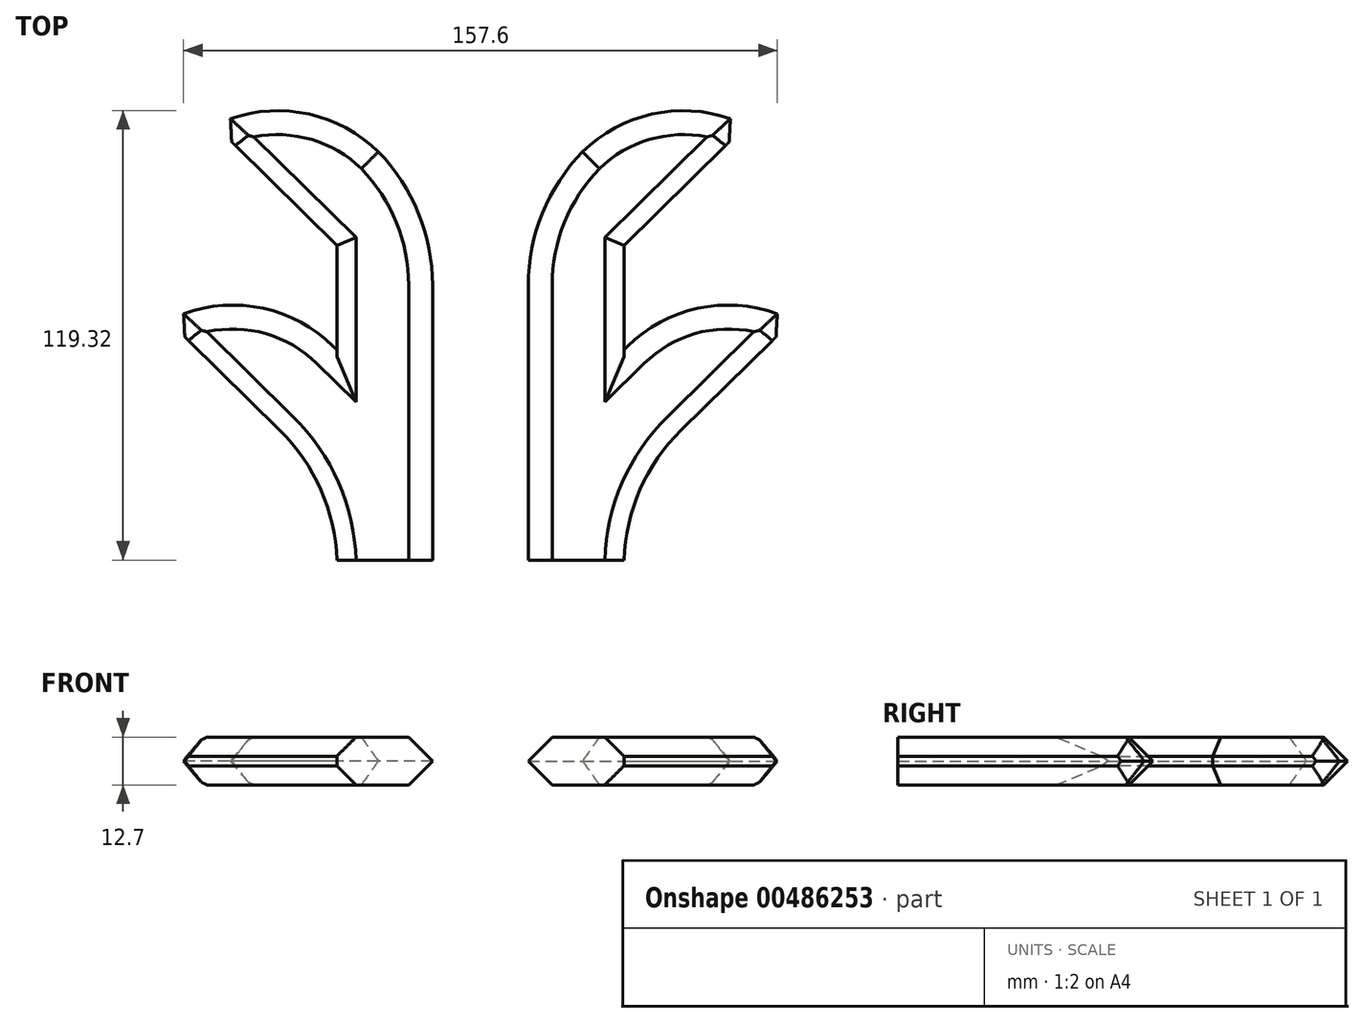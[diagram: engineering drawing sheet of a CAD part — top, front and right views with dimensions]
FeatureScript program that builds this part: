
annotation { "Feature Type Name" : "Feature", "Feature Type Description" : "" }
export const myFeature = defineFeature(function(context is Context, id is Id, definition is map)
    precondition{}
    {
        {
            var Q0;
            Q0=qCreatedBy(makeId("Top.planeOp"),FACE);
            var sketch = newSketch(context, id + "F0", { "sketchPlane" : qUnion([Q0])});
            skLineSegment(sketch, "E0.0", {"start": v(12.7, 94.22) * mm, "end": v(-27.32, 133.57) * mm});
            skLineSegment(sketch, "E1.0", {"start": v(-12.7, 83.58) * mm, "end": v(-45.13, 115.46) * mm});
            skLineSegment(sketch, "E2.0", {"start": v(12.7, 0) * mm, "end": v(12.7, 94.22) * mm});
            skLineSegment(sketch, "E3.0", {"start": v(-12.7, 0) * mm, "end": v(-12.7, 19.58) * mm});
            skLineSegment(sketch, "E4.0", {"start": v(-12.7, 55.85) * mm, "end": v(-39.37, 82.07) * mm});
            skLineSegment(sketch, "E5.0", {"start": v(-12.7, 19.58) * mm, "end": v(-57.5, 63.62) * mm});
            skLineSegment(sketch, "E6", {"start": v(-45.13, 115.46) * mm, "end": v(-27.32, 133.57) * mm});
            skLineSegment(sketch, "E7", {"start": v(-12.7, 0) * mm, "end": v(12.7, 0) * mm});
            skLineSegment(sketch, "E8.trimOffspring", {"start": v(-12.7, 55.85) * mm, "end": v(-12.7, 83.58) * mm});
            skLineSegment(sketch, "E9.0", {"start": v(-57.5, 63.62) * mm, "end": v(-39.37, 82.07) * mm});
            skSolve(sketch);
        }
        {
            var Q0;
            Q0=makeQuery(id+"F0.imprint","IMPRINT",FACE,{"disambiguationData":[TD([[makeQuery(id+"F0.imprint","IMPRINT",EDGE,{"derivedFrom":sQuery(id+"F0.wireOp",EDGE,"E0.0")}),1.0]])]});
            extrude(context, id + "F1", {"entities" : qUnion([Q0]), "depth" : 12.7 * mm});
        }
        {
            var Q0;
            Q0=makeQuery(id+"F1.opExtrude","SWEPT_EDGE",EDGE,{"disambiguationData":[OSD([sQuery(id+"F0.wireOp",EDGE,"E4.0"),sQuery(id+"F0.wireOp",EDGE,"E9.0")])]});
            var Q1;
            Q1=makeQuery(id+"F1.opExtrude","SWEPT_EDGE",EDGE,{"disambiguationData":[OSD([sQuery(id+"F0.wireOp",EDGE,"E0.0"),sQuery(id+"F0.wireOp",EDGE,"E6")])]});
            fillet(context, id + "F2", {"entities" : qUnion([Q0, Q1]), "radius" : 38.1 * mm, "tangentPropagation" : true, "allowEdgeOverflow" : false});
        }
        {
            var Q0;
            Q0=makeQuery(id+"F1.opExtrude","SWEPT_EDGE",EDGE,{"disambiguationData":[OSD([sQuery(id+"F0.wireOp",EDGE,"E3.0"),sQuery(id+"F0.wireOp",EDGE,"E5.0")])]});
            var Q1;
            Q1=makeQuery(id+"F1.opExtrude","SWEPT_EDGE",EDGE,{"disambiguationData":[OSD([sQuery(id+"F0.wireOp",EDGE,"E0.0"),sQuery(id+"F0.wireOp",EDGE,"E2.0")])]});
            fillet(context, id + "F3", {"entities" : qUnion([Q0, Q1]), "radius" : 50.8 * mm, "tangentPropagation" : true, "allowEdgeOverflow" : false});
        }
        {
            var Q0;
            {var subQ0=sQuery(id+"F0.wireOp",EDGE,"E9.0");var subQ1=sQuery(id+"F0.wireOp",EDGE,"E4.0");Q0=makeQuery(id+"F2.opFillet","BLEND_EDGE",EDGE,{"blendedFrom":[makeQuery(id+"F1.opExtrude","SWEPT_EDGE",EDGE,{"disambiguationData":[OSD([subQ1,subQ0])]}),makeQuery(id+"F1.opExtrude","CAP_FACE",FACE,{"disambiguationData":[OSD([sQuery(id+"F0.wireOp",EDGE,"E0.0"),sQuery(id+"F0.wireOp",EDGE,"E1.0"),sQuery(id+"F0.wireOp",EDGE,"E2.0"),sQuery(id+"F0.wireOp",EDGE,"E3.0"),subQ1,sQuery(id+"F0.wireOp",EDGE,"E5.0"),sQuery(id+"F0.wireOp",EDGE,"E6"),sQuery(id+"F0.wireOp",EDGE,"E7"),sQuery(id+"F0.wireOp",EDGE,"E8.trimOffspring"),subQ0])],"isStart":false})],"blendedInto":[makeQuery(id+"F1.opExtrude","CAP_FACE",FACE,{"disambiguationData":[OSD([sQuery(id+"F0.wireOp",EDGE,"E0.0"),sQuery(id+"F0.wireOp",EDGE,"E1.0"),sQuery(id+"F0.wireOp",EDGE,"E2.0"),sQuery(id+"F0.wireOp",EDGE,"E3.0"),subQ1,sQuery(id+"F0.wireOp",EDGE,"E5.0"),sQuery(id+"F0.wireOp",EDGE,"E6"),sQuery(id+"F0.wireOp",EDGE,"E7"),sQuery(id+"F0.wireOp",EDGE,"E8.trimOffspring"),subQ0])],"isStart":false})]});}
            var Q1;
            {var subQ0=sQuery(id+"F0.wireOp",EDGE,"E9.0");var subQ1=sQuery(id+"F0.wireOp",EDGE,"E4.0");Q1=makeQuery(id+"F2.opFillet","BLEND_EDGE",EDGE,{"blendedFrom":[makeQuery(id+"F1.opExtrude","SWEPT_EDGE",EDGE,{"disambiguationData":[OSD([subQ1,subQ0])]}),makeQuery(id+"F1.opExtrude","CAP_FACE",FACE,{"disambiguationData":[OSD([sQuery(id+"F0.wireOp",EDGE,"E0.0"),sQuery(id+"F0.wireOp",EDGE,"E1.0"),sQuery(id+"F0.wireOp",EDGE,"E2.0"),sQuery(id+"F0.wireOp",EDGE,"E3.0"),subQ1,sQuery(id+"F0.wireOp",EDGE,"E5.0"),sQuery(id+"F0.wireOp",EDGE,"E6"),sQuery(id+"F0.wireOp",EDGE,"E7"),sQuery(id+"F0.wireOp",EDGE,"E8.trimOffspring"),subQ0])],"isStart":true})],"blendedInto":[makeQuery(id+"F1.opExtrude","CAP_FACE",FACE,{"disambiguationData":[OSD([sQuery(id+"F0.wireOp",EDGE,"E0.0"),sQuery(id+"F0.wireOp",EDGE,"E1.0"),sQuery(id+"F0.wireOp",EDGE,"E2.0"),sQuery(id+"F0.wireOp",EDGE,"E3.0"),subQ1,sQuery(id+"F0.wireOp",EDGE,"E5.0"),sQuery(id+"F0.wireOp",EDGE,"E6"),sQuery(id+"F0.wireOp",EDGE,"E7"),sQuery(id+"F0.wireOp",EDGE,"E8.trimOffspring"),subQ0])],"isStart":true})]});}
            var Q2;
            {var subQ0=sQuery(id+"F0.wireOp",EDGE,"E6");var subQ1=sQuery(id+"F0.wireOp",EDGE,"E0.0");Q2=makeQuery(id+"F2.opFillet","BLEND_EDGE",EDGE,{"blendedFrom":[makeQuery(id+"F1.opExtrude","SWEPT_EDGE",EDGE,{"disambiguationData":[OSD([subQ1,subQ0])]}),makeQuery(id+"F1.opExtrude","CAP_FACE",FACE,{"disambiguationData":[OSD([subQ1,sQuery(id+"F0.wireOp",EDGE,"E1.0"),sQuery(id+"F0.wireOp",EDGE,"E2.0"),sQuery(id+"F0.wireOp",EDGE,"E3.0"),sQuery(id+"F0.wireOp",EDGE,"E4.0"),sQuery(id+"F0.wireOp",EDGE,"E5.0"),subQ0,sQuery(id+"F0.wireOp",EDGE,"E7"),sQuery(id+"F0.wireOp",EDGE,"E8.trimOffspring"),sQuery(id+"F0.wireOp",EDGE,"E9.0")])],"isStart":false})],"blendedInto":[makeQuery(id+"F1.opExtrude","CAP_FACE",FACE,{"disambiguationData":[OSD([subQ1,sQuery(id+"F0.wireOp",EDGE,"E1.0"),sQuery(id+"F0.wireOp",EDGE,"E2.0"),sQuery(id+"F0.wireOp",EDGE,"E3.0"),sQuery(id+"F0.wireOp",EDGE,"E4.0"),sQuery(id+"F0.wireOp",EDGE,"E5.0"),subQ0,sQuery(id+"F0.wireOp",EDGE,"E7"),sQuery(id+"F0.wireOp",EDGE,"E8.trimOffspring"),sQuery(id+"F0.wireOp",EDGE,"E9.0")])],"isStart":false})]});}
            var Q3;
            {var subQ0=sQuery(id+"F0.wireOp",EDGE,"E6");var subQ1=sQuery(id+"F0.wireOp",EDGE,"E0.0");Q3=makeQuery(id+"F2.opFillet","BLEND_EDGE",EDGE,{"blendedFrom":[makeQuery(id+"F1.opExtrude","SWEPT_EDGE",EDGE,{"disambiguationData":[OSD([subQ1,subQ0])]}),makeQuery(id+"F1.opExtrude","CAP_FACE",FACE,{"disambiguationData":[OSD([subQ1,sQuery(id+"F0.wireOp",EDGE,"E1.0"),sQuery(id+"F0.wireOp",EDGE,"E2.0"),sQuery(id+"F0.wireOp",EDGE,"E3.0"),sQuery(id+"F0.wireOp",EDGE,"E4.0"),sQuery(id+"F0.wireOp",EDGE,"E5.0"),subQ0,sQuery(id+"F0.wireOp",EDGE,"E7"),sQuery(id+"F0.wireOp",EDGE,"E8.trimOffspring"),sQuery(id+"F0.wireOp",EDGE,"E9.0")])],"isStart":true})],"blendedInto":[makeQuery(id+"F1.opExtrude","CAP_FACE",FACE,{"disambiguationData":[OSD([subQ1,sQuery(id+"F0.wireOp",EDGE,"E1.0"),sQuery(id+"F0.wireOp",EDGE,"E2.0"),sQuery(id+"F0.wireOp",EDGE,"E3.0"),sQuery(id+"F0.wireOp",EDGE,"E4.0"),sQuery(id+"F0.wireOp",EDGE,"E5.0"),subQ0,sQuery(id+"F0.wireOp",EDGE,"E7"),sQuery(id+"F0.wireOp",EDGE,"E8.trimOffspring"),sQuery(id+"F0.wireOp",EDGE,"E9.0")])],"isStart":true})]});}
            var Q4;
            Q4=makeQuery(id+"F1.opExtrude","CAP_EDGE",EDGE,{"disambiguationData":[OSD([sQuery(id+"F0.wireOp",EDGE,"E2.0")])],"isStart":false});
            var Q5;
            Q5=makeQuery(id+"F1.opExtrude","CAP_EDGE",EDGE,{"disambiguationData":[OSD([sQuery(id+"F0.wireOp",EDGE,"E2.0")])],"isStart":true});
            var Q6;
            {var subQ0=sQuery(id+"F0.wireOp",EDGE,"E2.0");var subQ1=sQuery(id+"F0.wireOp",EDGE,"E0.0");Q6=makeQuery(id+"F3.opFillet","BLEND_EDGE",EDGE,{"blendedFrom":[makeQuery(id+"F1.opExtrude","SWEPT_EDGE",EDGE,{"disambiguationData":[OSD([subQ1,subQ0])]}),makeQuery(id+"F1.opExtrude","CAP_FACE",FACE,{"disambiguationData":[OSD([subQ1,sQuery(id+"F0.wireOp",EDGE,"E1.0"),subQ0,sQuery(id+"F0.wireOp",EDGE,"E3.0"),sQuery(id+"F0.wireOp",EDGE,"E4.0"),sQuery(id+"F0.wireOp",EDGE,"E5.0"),sQuery(id+"F0.wireOp",EDGE,"E6"),sQuery(id+"F0.wireOp",EDGE,"E7"),sQuery(id+"F0.wireOp",EDGE,"E8.trimOffspring"),sQuery(id+"F0.wireOp",EDGE,"E9.0")])],"isStart":false})],"blendedInto":[makeQuery(id+"F1.opExtrude","CAP_FACE",FACE,{"disambiguationData":[OSD([subQ1,sQuery(id+"F0.wireOp",EDGE,"E1.0"),subQ0,sQuery(id+"F0.wireOp",EDGE,"E3.0"),sQuery(id+"F0.wireOp",EDGE,"E4.0"),sQuery(id+"F0.wireOp",EDGE,"E5.0"),sQuery(id+"F0.wireOp",EDGE,"E6"),sQuery(id+"F0.wireOp",EDGE,"E7"),sQuery(id+"F0.wireOp",EDGE,"E8.trimOffspring"),sQuery(id+"F0.wireOp",EDGE,"E9.0")])],"isStart":false})]});}
            var Q7;
            {var subQ0=sQuery(id+"F0.wireOp",EDGE,"E2.0");var subQ1=sQuery(id+"F0.wireOp",EDGE,"E0.0");Q7=makeQuery(id+"F3.opFillet","BLEND_EDGE",EDGE,{"blendedFrom":[makeQuery(id+"F1.opExtrude","SWEPT_EDGE",EDGE,{"disambiguationData":[OSD([subQ1,subQ0])]}),makeQuery(id+"F1.opExtrude","CAP_FACE",FACE,{"disambiguationData":[OSD([subQ1,sQuery(id+"F0.wireOp",EDGE,"E1.0"),subQ0,sQuery(id+"F0.wireOp",EDGE,"E3.0"),sQuery(id+"F0.wireOp",EDGE,"E4.0"),sQuery(id+"F0.wireOp",EDGE,"E5.0"),sQuery(id+"F0.wireOp",EDGE,"E6"),sQuery(id+"F0.wireOp",EDGE,"E7"),sQuery(id+"F0.wireOp",EDGE,"E8.trimOffspring"),sQuery(id+"F0.wireOp",EDGE,"E9.0")])],"isStart":true})],"blendedInto":[makeQuery(id+"F1.opExtrude","CAP_FACE",FACE,{"disambiguationData":[OSD([subQ1,sQuery(id+"F0.wireOp",EDGE,"E1.0"),subQ0,sQuery(id+"F0.wireOp",EDGE,"E3.0"),sQuery(id+"F0.wireOp",EDGE,"E4.0"),sQuery(id+"F0.wireOp",EDGE,"E5.0"),sQuery(id+"F0.wireOp",EDGE,"E6"),sQuery(id+"F0.wireOp",EDGE,"E7"),sQuery(id+"F0.wireOp",EDGE,"E8.trimOffspring"),sQuery(id+"F0.wireOp",EDGE,"E9.0")])],"isStart":true})]});}
            chamfer(context, id + "F4", {"entities" : qUnion([Q0, Q1, Q2, Q3, Q4, Q5, Q6, Q7]), "width" : 6.35 * mm, "tangentPropagation" : true});
        }
        {
            var Q0;
            {var subQ0=sQuery(id+"F0.wireOp",EDGE,"E1.0");var subQ1=sQuery(id+"F0.wireOp",EDGE,"E6");var subQ2=sQuery(id+"F0.wireOp",EDGE,"E0.0");Q0=makeQuery(id+"F4.opChamfer","BLEND_EDGE",EDGE,{"blendedFrom":[makeQuery(id+"F2.opFillet","BLEND_EDGE",EDGE,{"blendedFrom":[makeQuery(id+"F1.opExtrude","SWEPT_EDGE",EDGE,{"disambiguationData":[OSD([subQ2,subQ1])]}),makeQuery(id+"F1.opExtrude","CAP_FACE",FACE,{"disambiguationData":[OSD([subQ2,subQ0,sQuery(id+"F0.wireOp",EDGE,"E2.0"),sQuery(id+"F0.wireOp",EDGE,"E3.0"),sQuery(id+"F0.wireOp",EDGE,"E4.0"),sQuery(id+"F0.wireOp",EDGE,"E5.0"),subQ1,sQuery(id+"F0.wireOp",EDGE,"E7"),sQuery(id+"F0.wireOp",EDGE,"E8.trimOffspring"),sQuery(id+"F0.wireOp",EDGE,"E9.0")])],"isStart":false})],"blendedInto":[makeQuery(id+"F1.opExtrude","CAP_FACE",FACE,{"disambiguationData":[OSD([subQ2,subQ0,sQuery(id+"F0.wireOp",EDGE,"E2.0"),sQuery(id+"F0.wireOp",EDGE,"E3.0"),sQuery(id+"F0.wireOp",EDGE,"E4.0"),sQuery(id+"F0.wireOp",EDGE,"E5.0"),subQ1,sQuery(id+"F0.wireOp",EDGE,"E7"),sQuery(id+"F0.wireOp",EDGE,"E8.trimOffspring"),sQuery(id+"F0.wireOp",EDGE,"E9.0")])],"isStart":false})]}),makeQuery(id+"F1.opExtrude","SWEPT_FACE",FACE,{"disambiguationData":[OSD([subQ0])]})],"blendedInto":[makeQuery(id+"F1.opExtrude","SWEPT_FACE",FACE,{"disambiguationData":[OSD([subQ0])]})]});}
            var Q1;
            {var subQ0=sQuery(id+"F0.wireOp",EDGE,"E1.0");var subQ1=sQuery(id+"F0.wireOp",EDGE,"E6");var subQ2=sQuery(id+"F0.wireOp",EDGE,"E0.0");Q1=makeQuery(id+"F4.opChamfer","BLEND_EDGE",EDGE,{"blendedFrom":[makeQuery(id+"F2.opFillet","BLEND_EDGE",EDGE,{"blendedFrom":[makeQuery(id+"F1.opExtrude","SWEPT_EDGE",EDGE,{"disambiguationData":[OSD([subQ2,subQ1])]}),makeQuery(id+"F1.opExtrude","CAP_FACE",FACE,{"disambiguationData":[OSD([subQ2,subQ0,sQuery(id+"F0.wireOp",EDGE,"E2.0"),sQuery(id+"F0.wireOp",EDGE,"E3.0"),sQuery(id+"F0.wireOp",EDGE,"E4.0"),sQuery(id+"F0.wireOp",EDGE,"E5.0"),subQ1,sQuery(id+"F0.wireOp",EDGE,"E7"),sQuery(id+"F0.wireOp",EDGE,"E8.trimOffspring"),sQuery(id+"F0.wireOp",EDGE,"E9.0")])],"isStart":true})],"blendedInto":[makeQuery(id+"F1.opExtrude","CAP_FACE",FACE,{"disambiguationData":[OSD([subQ2,subQ0,sQuery(id+"F0.wireOp",EDGE,"E2.0"),sQuery(id+"F0.wireOp",EDGE,"E3.0"),sQuery(id+"F0.wireOp",EDGE,"E4.0"),sQuery(id+"F0.wireOp",EDGE,"E5.0"),subQ1,sQuery(id+"F0.wireOp",EDGE,"E7"),sQuery(id+"F0.wireOp",EDGE,"E8.trimOffspring"),sQuery(id+"F0.wireOp",EDGE,"E9.0")])],"isStart":true})]}),makeQuery(id+"F1.opExtrude","SWEPT_FACE",FACE,{"disambiguationData":[OSD([subQ0])]})],"blendedInto":[makeQuery(id+"F1.opExtrude","SWEPT_FACE",FACE,{"disambiguationData":[OSD([subQ0])]})]});}
            var Q2;
            {var subQ0=sQuery(id+"F0.wireOp",EDGE,"E5.0");var subQ1=sQuery(id+"F0.wireOp",EDGE,"E9.0");var subQ2=sQuery(id+"F0.wireOp",EDGE,"E4.0");Q2=makeQuery(id+"F4.opChamfer","BLEND_EDGE",EDGE,{"blendedFrom":[makeQuery(id+"F2.opFillet","BLEND_EDGE",EDGE,{"blendedFrom":[makeQuery(id+"F1.opExtrude","SWEPT_EDGE",EDGE,{"disambiguationData":[OSD([subQ2,subQ1])]}),makeQuery(id+"F1.opExtrude","CAP_FACE",FACE,{"disambiguationData":[OSD([sQuery(id+"F0.wireOp",EDGE,"E0.0"),sQuery(id+"F0.wireOp",EDGE,"E1.0"),sQuery(id+"F0.wireOp",EDGE,"E2.0"),sQuery(id+"F0.wireOp",EDGE,"E3.0"),subQ2,subQ0,sQuery(id+"F0.wireOp",EDGE,"E6"),sQuery(id+"F0.wireOp",EDGE,"E7"),sQuery(id+"F0.wireOp",EDGE,"E8.trimOffspring"),subQ1])],"isStart":false})],"blendedInto":[makeQuery(id+"F1.opExtrude","CAP_FACE",FACE,{"disambiguationData":[OSD([sQuery(id+"F0.wireOp",EDGE,"E0.0"),sQuery(id+"F0.wireOp",EDGE,"E1.0"),sQuery(id+"F0.wireOp",EDGE,"E2.0"),sQuery(id+"F0.wireOp",EDGE,"E3.0"),subQ2,subQ0,sQuery(id+"F0.wireOp",EDGE,"E6"),sQuery(id+"F0.wireOp",EDGE,"E7"),sQuery(id+"F0.wireOp",EDGE,"E8.trimOffspring"),subQ1])],"isStart":false})]}),makeQuery(id+"F1.opExtrude","SWEPT_FACE",FACE,{"disambiguationData":[OSD([subQ0])]})],"blendedInto":[makeQuery(id+"F1.opExtrude","SWEPT_FACE",FACE,{"disambiguationData":[OSD([subQ0])]})]});}
            var Q3;
            {var subQ0=sQuery(id+"F0.wireOp",EDGE,"E5.0");var subQ1=sQuery(id+"F0.wireOp",EDGE,"E9.0");var subQ2=sQuery(id+"F0.wireOp",EDGE,"E4.0");Q3=makeQuery(id+"F4.opChamfer","BLEND_EDGE",EDGE,{"blendedFrom":[makeQuery(id+"F2.opFillet","BLEND_EDGE",EDGE,{"blendedFrom":[makeQuery(id+"F1.opExtrude","SWEPT_EDGE",EDGE,{"disambiguationData":[OSD([subQ2,subQ1])]}),makeQuery(id+"F1.opExtrude","CAP_FACE",FACE,{"disambiguationData":[OSD([sQuery(id+"F0.wireOp",EDGE,"E0.0"),sQuery(id+"F0.wireOp",EDGE,"E1.0"),sQuery(id+"F0.wireOp",EDGE,"E2.0"),sQuery(id+"F0.wireOp",EDGE,"E3.0"),subQ2,subQ0,sQuery(id+"F0.wireOp",EDGE,"E6"),sQuery(id+"F0.wireOp",EDGE,"E7"),sQuery(id+"F0.wireOp",EDGE,"E8.trimOffspring"),subQ1])],"isStart":true})],"blendedInto":[makeQuery(id+"F1.opExtrude","CAP_FACE",FACE,{"disambiguationData":[OSD([sQuery(id+"F0.wireOp",EDGE,"E0.0"),sQuery(id+"F0.wireOp",EDGE,"E1.0"),sQuery(id+"F0.wireOp",EDGE,"E2.0"),sQuery(id+"F0.wireOp",EDGE,"E3.0"),subQ2,subQ0,sQuery(id+"F0.wireOp",EDGE,"E6"),sQuery(id+"F0.wireOp",EDGE,"E7"),sQuery(id+"F0.wireOp",EDGE,"E8.trimOffspring"),subQ1])],"isStart":true})]}),makeQuery(id+"F1.opExtrude","SWEPT_FACE",FACE,{"disambiguationData":[OSD([subQ0])]})],"blendedInto":[makeQuery(id+"F1.opExtrude","SWEPT_FACE",FACE,{"disambiguationData":[OSD([subQ0])]})]});}
            chamfer(context, id + "F5", {"entities" : qUnion([Q0, Q1, Q2, Q3]), "width" : 3.17 * mm, "tangentPropagation" : true});
        }
        {
            var Q0;
            Q0=makeQuery(id+"F1.opExtrude","CAP_EDGE",EDGE,{"disambiguationData":[OSD([sQuery(id+"F0.wireOp",EDGE,"E1.0")])],"isStart":false});
            var Q1;
            Q1=makeQuery(id+"F1.opExtrude","CAP_EDGE",EDGE,{"disambiguationData":[OSD([sQuery(id+"F0.wireOp",EDGE,"E1.0")])],"isStart":true});
            var Q2;
            Q2=makeQuery(id+"F1.opExtrude","CAP_EDGE",EDGE,{"disambiguationData":[OSD([sQuery(id+"F0.wireOp",EDGE,"E8.trimOffspring")])],"isStart":false});
            var Q3;
            Q3=makeQuery(id+"F1.opExtrude","CAP_EDGE",EDGE,{"disambiguationData":[OSD([sQuery(id+"F0.wireOp",EDGE,"E8.trimOffspring")])],"isStart":true});
            var Q4;
            Q4=makeQuery(id+"F1.opExtrude","CAP_EDGE",EDGE,{"disambiguationData":[OSD([sQuery(id+"F0.wireOp",EDGE,"E5.0")])],"isStart":false});
            var Q5;
            Q5=makeQuery(id+"F1.opExtrude","CAP_EDGE",EDGE,{"disambiguationData":[OSD([sQuery(id+"F0.wireOp",EDGE,"E5.0")])],"isStart":true});
            chamfer(context, id + "F6", {"entities" : qUnion([Q0, Q1, Q2, Q3, Q4, Q5]), "width" : 5.08 * mm, "tangentPropagation" : true});
        }
        {
            var Q0;
            Q0=qCreatedBy(makeId("Right.planeOp"),FACE);
            cPlane(context, id + "F7", {"entities" : qUnion([Q0]), "cplaneType" : CPlaneType.OFFSET, "offset" : 25.4 * mm, "width" : 152.4 * mm, "height" : 152.4 * mm});
        }
        {
            var Q0;
            Q0=makeQuery(id+"F1.opExtrude","SWEPT_BODY",BODY,{"disambiguationData":[OSD([sQuery(id+"F0.wireOp",EDGE,"E0.0"),sQuery(id+"F0.wireOp",EDGE,"E1.0"),sQuery(id+"F0.wireOp",EDGE,"E2.0"),sQuery(id+"F0.wireOp",EDGE,"E3.0"),sQuery(id+"F0.wireOp",EDGE,"E4.0"),sQuery(id+"F0.wireOp",EDGE,"E5.0"),sQuery(id+"F0.wireOp",EDGE,"E6"),sQuery(id+"F0.wireOp",EDGE,"E7"),sQuery(id+"F0.wireOp",EDGE,"E8.trimOffspring"),sQuery(id+"F0.wireOp",EDGE,"E9.0")])]});
            var Q1;
            Q1=qCreatedBy(id+"F7.planeOp",FACE);
            mirror(context, id + "F8", {"entities" : qUnion([Q0]), "mirrorPlane" : qUnion([Q1])});
        }
    });
